# Revit family: QF_Vivreau_V3-205
name_source: partatom
category: Specialty Equipment
revit_build: Autodesk Revit 2018 (Build: 20190510_1515(x64)
units: mm (PartAtom-declared; Revit-internal decimal feet)

## family parameters
Always vertical = Yes
Cut with Voids When Loaded = No
OmniClass Number = 23.40.40.14.24
OmniClass Title = Food Dispensing Equipment
Part Type = Normal
Room Calculation Point = No
Round Connector Dimension = Use Diameter
Shared = No
Work Plane-Based = No

## types (1)
- QF_Vivreau_V3-205
    Apparent Power = 1320 VA
    Assembly Code = E1090320
    BTUH = 0.0 Btu/h
    CSI MasterFormat = 11 46 00
    Cabinet Height = 2' - 6"
    Cabinet Width = 2' - 0"
    Cold Water Connection Height = 2' - 0"
    Cold Water Flow = 1 GPM
    Cold Water Maximum Pressure = 90.00 psi
    Cold Water Minimum Pressure = 50.00 psi
    Cold Water RI Height = 0' - 0"
    Cold Water Size = 1"
    Cold Water Temperature Recommended = 60 °F
    Conn Conduit = No
    Conn Plug = 5-20P
    Cycle = 60 Hz
    Description = Water Dispenser
    Elec Conn Connection Height = 2' - 0"
    Elec Conn RI Height = 0' - 0"
    Electric Connection Type = Plug
    Electrical Remarks = Requires One (1) 20 Amp Electrical Receptacle (5-20R) GFCI Recommended
    FL Amps = 11 A
    Foodservice Equipment Identifier = Yes
    Identify Quantity as Lot = Yes
    Indirect Waste Connection Type = Vertical Stand Pipe
    Indirect Waste Flow = 0 GPM
    Indirect Waste Size = 1"
    Manufacturer = Vivreau
    Masterspec = Division 11
    Max Overcurrent Protection = 16 A
    Min Ckt Ampacity = 11 A
    Model = V3-205
    Number of Poles = 1
    Phase = 1
    Plumbing Connection Type = FNPT Ball Valve
    Plumbing Remarks = Cold Water Consumption Will Vary Based On Use, Indirect Waste Flow Willl Vary Based On Use
    Refrigerant Type = 134a
    Refrigerant Volume = 0.000220 kip
    Specification by Manufacturer = Vivreau Water Bottling System, mini bottler, dual tap, fully integrated undercounter, self-contained ice-bank refrigeration, advanced micro-filtered, chilled still & sparkling water, filter with filter head, CO2 cylinder (CO2 is customer supplied), CO2 regulator, stainless steel drip tray, removable nozzles, x1 20amp electrical receptacle (5-20 R) 120V 60Hz (8 amps), NEMA 5-20R, ETL, NSF (for indoor use only)
    URL = https://vivreauwater.com
    URL Cutsheet = https://vivreauwater.com
    Volts = 120 V
    Waste Water Discharge Temperature = 0 °F
    Watts = 1320 W
    Weight in Pounds = 140

## geometry (parser evidence)
native form markers: Sweep x19
no freeform markers — native parametric forms only
